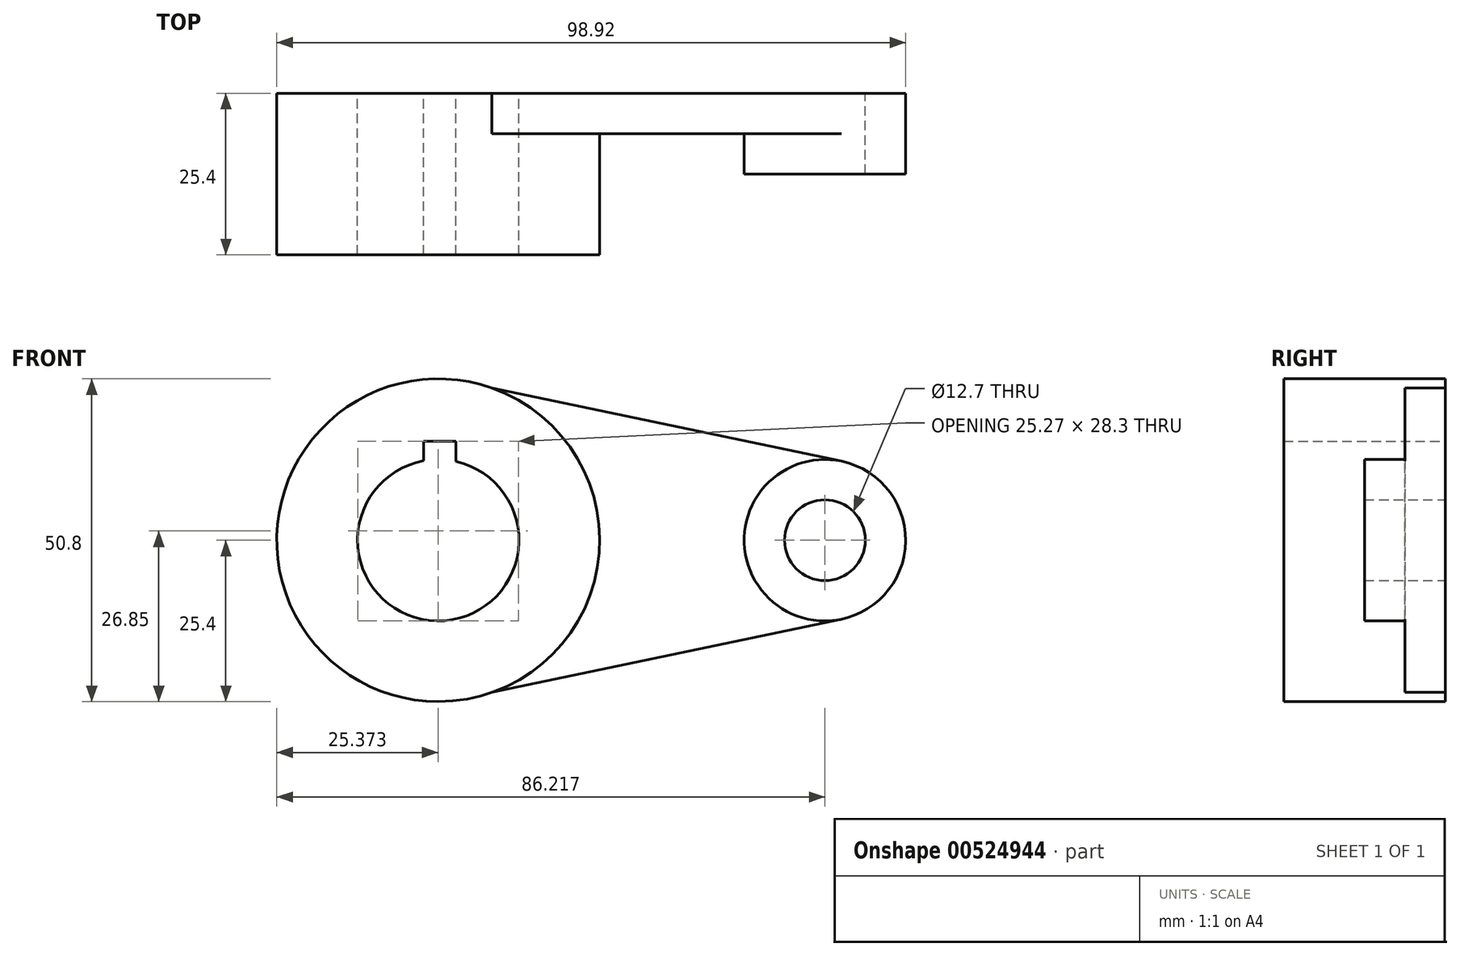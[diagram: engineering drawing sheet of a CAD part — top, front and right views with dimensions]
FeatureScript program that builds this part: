
annotation { "Feature Type Name" : "Feature", "Feature Type Description" : "" }
export const myFeature = defineFeature(function(context is Context, id is Id, definition is map)
    precondition{}
    {
        {
            var Q0;
            Q0=qCreatedBy(makeId("Front.planeOp"),FACE);
            var sketch = newSketch(context, id + "F0", { "sketchPlane" : qUnion([Q0])});
            skCircle(sketch, "E0", {"center": v(-34.08, 0) * mm, "radius": 25.4 * mm});
            skCircle(sketch, "E1", {"center": v(-34.08, 0) * mm, "radius": 12.7 * mm});
            skCircle(sketch, "E2", {"center": v(26.74, 0) * mm, "radius": 12.7 * mm});
            skCircle(sketch, "E3", {"center": v(26.74, 0) * mm, "radius": 6.35 * mm});
            skLineSegment(sketch, "E4", {"start": v(-25.62, 23.95) * mm, "end": v(29.34, 12.43) * mm});
            skLineSegment(sketch, "E5", {"start": v(-25.62, -23.95) * mm, "end": v(29.34, -12.43) * mm});
            skLineSegment(sketch, "E6.bottom", {"start": v(-36.4, 15.6) * mm, "end": v(-31.31, 15.6) * mm});
            skLineSegment(sketch, "E6.top", {"start": v(-36.4, 10.52) * mm, "end": v(-31.31, 10.52) * mm});
            skLineSegment(sketch, "E6.left", {"start": v(-36.4, 15.6) * mm, "end": v(-36.4, 10.52) * mm});
            skLineSegment(sketch, "E6.right", {"start": v(-31.31, 15.6) * mm, "end": v(-31.31, 10.52) * mm});
            skSolve(sketch);
        }
        {
            var Q0;
            {var subQ0=sQuery(id+"F0.wireOp",EDGE,"E6.bottom");Q0=makeQuery(id+"F0.imprint","IMPRINT",FACE,{"disambiguationData":[TD([[makeQuery(id+"F0.imprint","IMPRINT",EDGE,{"derivedFrom":subQ0}),1.0]])]});}
            extrude(context, id + "F1", {"entities" : qUnion([Q0]), "depth" : 25.4 * mm, "offsetDistance" : 25.4 * mm});
        }
        {
            var Q0;
            {var subQ0=sQuery(id+"F0.wireOp",EDGE,"E4");Q0=makeQuery(id+"F0.imprint","IMPRINT",FACE,{"disambiguationData":[TD([[makeQuery(id+"F0.imprint","IMPRINT",EDGE,{"derivedFrom":subQ0}),-1.0]])]});}
            extrude(context, id + "F2", {"entities" : qUnion([Q0]), "operationType" : NewBodyOperationType.ADD, "depth" : 6.35 * mm, "offsetDistance" : 25.4 * mm});
        }
        {
            var Q0;
            Q0=makeQuery(id+"F0.imprint","IMPRINT",FACE,{"disambiguationData":[TD([[makeQuery(id+"F0.imprint","IMPRINT",EDGE,{"derivedFrom":sQuery(id+"F0.wireOp",EDGE,"E3")}),-1.0]])]});
            extrude(context, id + "F3", {"entities" : qUnion([Q0]), "operationType" : NewBodyOperationType.ADD, "depth" : 12.7 * mm, "offsetDistance" : 25.4 * mm});
        }
    });
